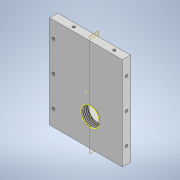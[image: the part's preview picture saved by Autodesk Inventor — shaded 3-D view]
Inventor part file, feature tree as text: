
AUTODESK INVENTOR PART (.ipt)
format: ipt  version: 2022.2 (Build 262287030, 287C)  size: 274,944 bytes
history: native  units: in
note: dims shown in document units (in); Inventor stores cm internally (conversion verified against a paired STEP export)
features: sketch x8, hole x5, extrude x1, plane x1, helix x1
ambient origin geometry x8: Origin, YZ Plane, XZ Plane, XY Plane, X Axis, Y Axis, Z Axis, Center Point
bodies: Solid1 (feature_tree)
feature tree (16):
  extrude  "Extrusion1"  Depth=4.5276in
  hole  "Hole1"  [1 undecoded]
  hole  "Hole2"  [1 undecoded]
  hole  "Hole3"  [1 undecoded]
  hole  "Hole4"  [1 undecoded]
  hole  "Hole5"  [1 undecoded]
  sketch  "Sketch9"  dims[d38=0.7874in d40=1.9685in d41=0.3937in d43=0.3937in]
  plane  "Work Plane1"
  helix  "Coil1"  [1 undecoded]
  sketch  "Sketch1"  dims[d0=3.5433in d1=4.5276in]
  sketch  "Sketch2"  dims[d2=0.3937in d3=0.0in d4=0.7874in]
  sketch  "Sketch3"  dims[d5=0.1969in d6=1.1811in d8=1.4764in d9=0.3937in d11=0.3937in]
  sketch  "Sketch4"  dims[d13=0.125in d14=0.2953in d15=0.1476in d16=0.0984in d17=90.0deg d18=0.1969in d19=0.0in d20=0.9843in]
  sketch  "Sketch5"  dims[d21=0.1969in d22=0.7874in d24=1.9685in d25=0.3937in d27=0.3937in]
  sketch  "Sketch8"  dims[d29=0.125in d30=0.2953in d31=0.1476in d32=0.0984in d33=90.0deg d34=0.1969in d35=0.0in d36=0.9843in d37=0.1969in]
  sketch  "Sketch10"  dims[d45=0.125in d46=0.2953in d47=0.1476in d48=0.0984in d49=90.0deg d50=0.1969in d51=0.0in d52=0.1969in d53=0.7874in d54=1.1811in d56=1.4764in d57=0.3937in d59=0.3937in d61=0.125in d62=0.2953in d63=0.1476in d64=0.0984in d65=90.0deg d66=0.1969in d67=0.0in d79=0.9055in d80=2.0819in d81=0.1476in d82=0.0984in d83=90.0deg d84=0.3937in d85=0.8108in d86=0.4528in d94=0.0787in d95=0.0394in d96=0.0in d97=0.3543in d98=0.0787in d99=0.3937in d100=2.3622in d101=0.0in d102=90.0deg d103=90.0deg d104=0.0in d105=0.0in d106=0.0079in]
note: 6 required parameter values undecoded (feature->parameter linkage not recoverable at this tier; creation-order binding heuristic only, values carry confidence <= 0.55)
